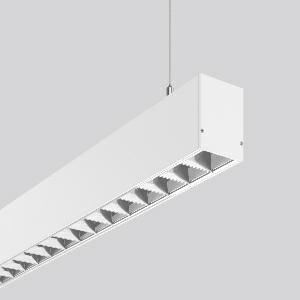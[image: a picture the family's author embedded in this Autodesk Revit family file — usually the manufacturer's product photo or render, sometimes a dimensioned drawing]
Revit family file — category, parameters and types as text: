
# Revit family: less_is_more_50_312345_002_83e4
name_source: partatom
category: Lighting Fixtures
units: mm (PartAtom-declared; Revit-internal decimal feet)

## family parameters
Cut with Voids When Loaded = No
Host = Face
Light Source = No
Part Type = Normal
Room Calculation Point = No
Round Connector Dimension = Use Diameter
Shared = No

## types (1)
- LESS IS MORE 50 (1 x LED Modul 830, 8800 lm, 3000)
    Apparent Load = 76 VA
    CIE Flux Codes = 95 100 100 63 100
    Color Rendering = 80
    Color Temperature = 3000
    Default Elevation = 1800 mm
    Description = Series: LESS IS MORE 50
Linear pendant luminaire for aesthetically sophisticated lighting. Housing: extruded aluminium profile, powder-coated. End cap aluminium powder-coated. Canopy made of aluminium, powder-coated. Alea optical system: Reflector structure (ABS, Aluminium-coated, highly polished) with integrated diffuser made of non-yellowing plastic (PMMA) opal for glare-free light at the workstation (screen-compliant according to EN 12464-1). Direct 65%, indirect 35% light emission. Suitable for pendant. 2-point steel cable suspension freely positionable and infinitely height-adjustable. Special lengths available on request. LED unit with integrated converter interchangeable and removable. Suitable for through-wiring. With sensors or as a safety luminaire on request. 
Colour: traffic white, matt (RAL 9016)
Length: 1967 mm
Width: 57 mm
Height: 75 mm
Suspension length: 2000 mm
Lamp: LED
Socket: without socket
Colour temperature: 3000K
Colour rendering index (CRI): 80
Light source: LED
Socket lamp2: Without base
Colour temperature: 3000K
System power: 76 W
Rated luminous flux: 8800 lm
Luminous efficiency: 116 lm/W
Control gear: Regulated power supply
Control gear: Regulated power supply
Protection class: I
Type of protection: IP 20
    Height = 75 mm
    Lamp = 1 x LED Modul 830
    Lamp Light Flux = 8800 lm
    Lamp count = 1
    Length = 1967 mm
    Lifetime = 50000 h
    Luminous efficacy = 116 lm/W
    Manufacturer = RZB
    ModVariant = No
    Model = 312345.002
    Mounting Place = Ceiling
    Mounting Type = Pendant
    Number of Poles = 1
    OnlyDefault = Yes
    Power Factor = 1
    Product Name = LESS IS MORE 50
    Product group = Pendant LED linear luminaires
    ProductGroupID = 907
    Protection Class = Protection class I
    Protection Degree = IP 20
    RLX_Detail_Level = 1
    RLX_Emergency_Light_Flux = 0 lm
    RLX_Emergency_Type = 0
    RLX_Emergency_Type_DB = No
    RlxData = <blob elided: 37497 chars, md5=9cc93ac7>
    Socket = socket
    Standby Power = 0 W
    System Light Flux = 8800 lm
    System Power = 76 W
    Type Comments = Product without accessories
    Type Image = 312342.002.jpg
    URL = http://relux.com
    VarID = ---
    Voltage = 230 V
    Voltage Range = 220-240 V
    Weight = 0.00 kg
    Width = 57 mm

## geometry (parser evidence)
native form markers: Blend x4, Sweep x10
no freeform markers — native parametric forms only
